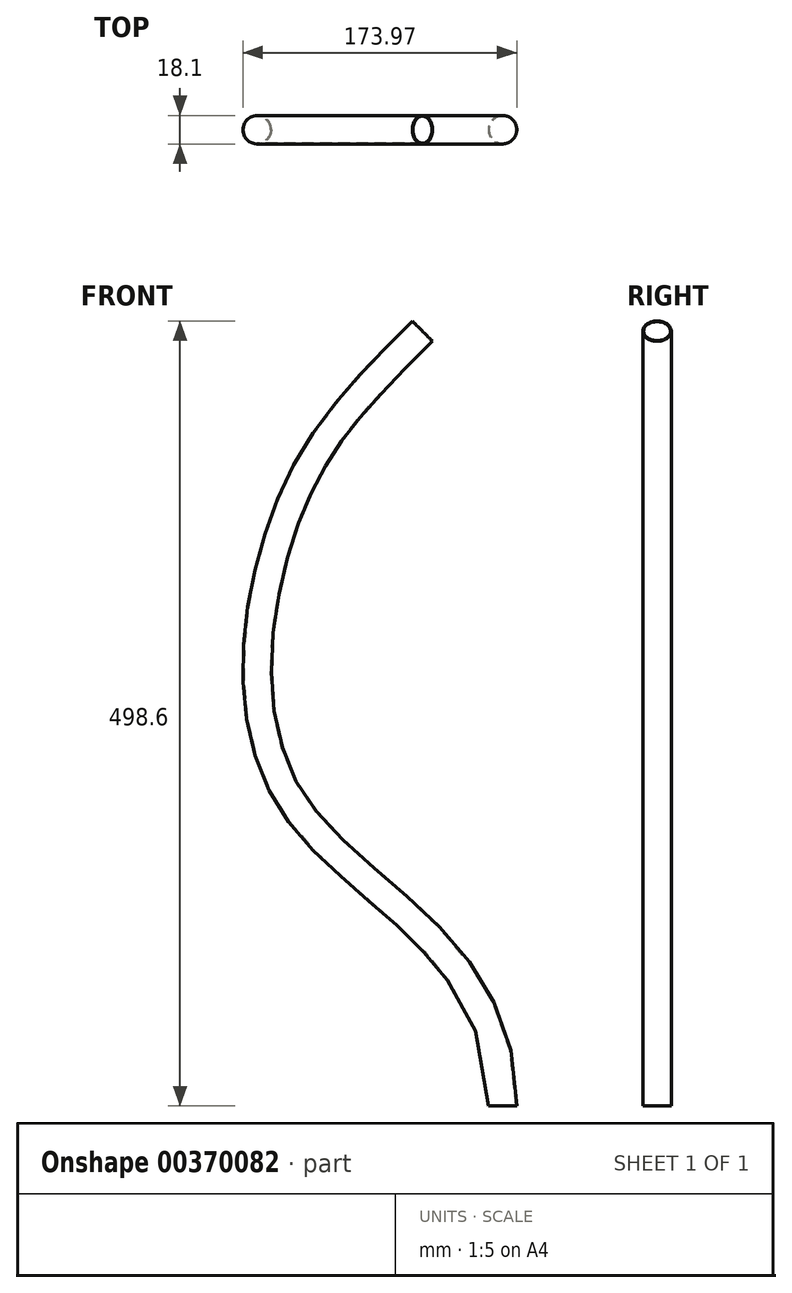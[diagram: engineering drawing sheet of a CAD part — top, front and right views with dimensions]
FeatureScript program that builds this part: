
annotation { "Feature Type Name" : "Feature", "Feature Type Description" : "" }
export const myFeature = defineFeature(function(context is Context, id is Id, definition is map)
    precondition{}
    {
        {
            var Q0;
            Q0=qCreatedBy(makeId("Front.planeOp"),FACE);
            var sketch = newSketch(context, id + "F0", { "sketchPlane" : qUnion([Q0])});
            skFitSpline(sketch, "E0", {"points": [v(0, 0) * mm, v(-450, 650) * mm, v(-450.65, 1268.56) * mm, v(-169.7, 1640.69) * mm], "startDerivative": vector(0, 2785.16) * mm, "endDerivative": vector(1420.91, 1420.91) * mm});
            skSolve(sketch);
        }
        {
            var Q0;
            Q0=qCreatedBy(makeId("Top.planeOp"),FACE);
            var sketch = newSketch(context, id + "F1", { "sketchPlane" : qUnion([Q0])});
            skCircle(sketch, "E1", {"center": v(0, 0) * mm, "radius": 30.15 * mm});
            skCircle(sketch, "E2", {"center": v(0, 0) * mm, "radius": 28.5 * mm});
            skSolve(sketch);
        }
        {
            var Q0;
            Q0=makeQuery(id+"F1.imprint","IMPRINT",FACE,{"disambiguationData":[TD([[makeQuery(id+"F1.imprint","IMPRINT",EDGE,{"derivedFrom":sQuery(id+"F1.wireOp",EDGE,"E1")}),1.0]])]});
            var Q1;
            Q1=sQuery(id+"F0.wireOp",EDGE,"E0");
            sweep(context, id + "F2", {"profiles" : qUnion([Q0]), "path" : qUnion([Q1])});
        }
        {
            var Q0;
            Q0=makeQuery(id+"F2.opSweep","SWEPT_BODY",BODY,{"disambiguationData":[OSD([sQuery(id+"F0.wireOp",EDGE,"E0"),sQuery(id+"F1.wireOp",EDGE,"E1"),sQuery(id+"F1.wireOp",EDGE,"E2")])]});
            var Q1;
            Q1=qCreatedBy(makeId("Origin.pointOp"),VERTEX);
            transform(context, id + "F3", {"entities" : qUnion([Q0]), "transformType" : TransformType.SCALE_UNIFORMLY, "scale" : 0.3, "scalePoint" : qUnion([Q1]), "makeCopy" : false});
        }
    });
